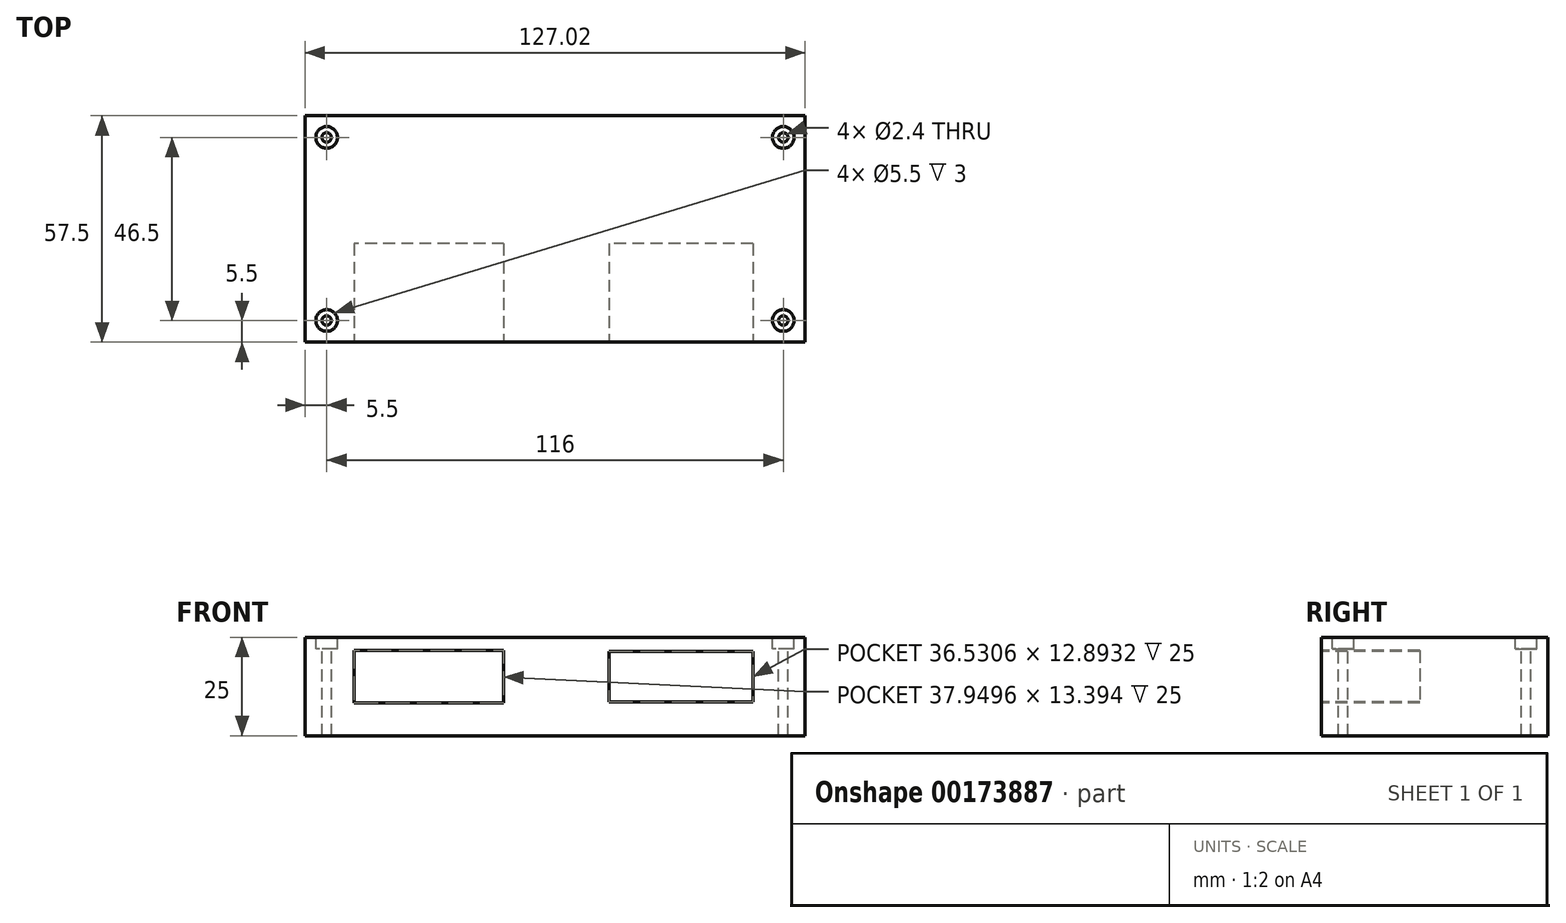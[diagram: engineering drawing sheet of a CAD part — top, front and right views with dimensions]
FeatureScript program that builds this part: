
annotation { "Feature Type Name" : "Feature", "Feature Type Description" : "" }
export const myFeature = defineFeature(function(context is Context, id is Id, definition is map)
    precondition{}
    {
        {
            var Q0;
            Q0=qCreatedBy(makeId("Top.planeOp"),FACE);
            var sketch = newSketch(context, id + "F0", { "sketchPlane" : qUnion([Q0])});
            skLineSegment(sketch, "E0.bottom", {"start": v(0, 0) * mm, "end": v(127.02, 0) * mm});
            skLineSegment(sketch, "E0.top", {"start": v(0, 57.5) * mm, "end": v(127.02, 57.5) * mm});
            skLineSegment(sketch, "E0.left", {"start": v(0, 0) * mm, "end": v(0, 57.5) * mm});
            skLineSegment(sketch, "E0.right", {"start": v(127.02, 0) * mm, "end": v(127.02, 57.5) * mm});
            skSolve(sketch);
        }
        {
            var Q0;
            Q0=makeQuery(id+"F0.imprint","IMPRINT",FACE,{"disambiguationData":[TD([[makeQuery(id+"F0.imprint","IMPRINT",EDGE,{"derivedFrom":sQuery(id+"F0.wireOp",EDGE,"E0.bottom")}),1.0]])]});
            extrude(context, id + "F1", {"entities" : qUnion([Q0]), "depth" : 25 * mm});
        }
        {
            var Q0;
            Q0=makeQuery(id+"F1.opExtrude","SWEPT_FACE",FACE,{"disambiguationData":[OSD([sQuery(id+"F0.wireOp",EDGE,"E0.bottom")])]});
            var sketch = newSketch(context, id + "F2", { "sketchPlane" : qUnion([Q0])});
            skLineSegment(sketch, "E1.bottom", {"start": v(50.47, 21.7) * mm, "end": v(12.53, 21.7) * mm});
            skLineSegment(sketch, "E1.top", {"start": v(50.47, 8.3) * mm, "end": v(12.53, 8.3) * mm});
            skLineSegment(sketch, "E1.left", {"start": v(50.47, 21.7) * mm, "end": v(50.47, 8.3) * mm});
            skLineSegment(sketch, "E1.right", {"start": v(12.53, 21.7) * mm, "end": v(12.53, 8.3) * mm});
            skPoint(sketch, "E1.middle", {"position": v(31.5, 15) * mm});
            skLineSegment(sketch, "E2.bottom", {"start": v(113.77, 21.45) * mm, "end": v(77.23, 21.45) * mm});
            skLineSegment(sketch, "E2.top", {"start": v(113.77, 8.55) * mm, "end": v(77.23, 8.55) * mm});
            skLineSegment(sketch, "E2.left", {"start": v(113.77, 21.45) * mm, "end": v(113.77, 8.55) * mm});
            skLineSegment(sketch, "E2.right", {"start": v(77.23, 21.45) * mm, "end": v(77.23, 8.55) * mm});
            skPoint(sketch, "E2.middle", {"position": v(95.5, 15) * mm});
            skSolve(sketch);
        }
        {
            var Q0;
            Q0 = qSketchRegion(id + "F2", true);
            extrude(context, id + "F3", {"entities" : qUnion([Q0]), "operationType" : NewBodyOperationType.REMOVE, "oppositeDirection" : true, "depth" : 25 * mm});
        }
        {
            var Q0;
            Q0=makeQuery(id+"F1.opExtrude","CAP_FACE",FACE,{"disambiguationData":[OSD([sQuery(id+"F0.wireOp",EDGE,"E0.bottom"),sQuery(id+"F0.wireOp",EDGE,"E0.top"),sQuery(id+"F0.wireOp",EDGE,"E0.left"),sQuery(id+"F0.wireOp",EDGE,"E0.right")])],"isStart":false});
            var sketch = newSketch(context, id + "F4", { "sketchPlane" : qUnion([Q0])});
            skLineSegment(sketch, "E3.bottom", {"start": v(0, 0) * mm, "end": v(8.5, 0) * mm});
            skLineSegment(sketch, "E3.top", {"start": v(0, 8.5) * mm, "end": v(8.5, 8.5) * mm});
            skLineSegment(sketch, "E3.left", {"start": v(0, 0) * mm, "end": v(0, 8.5) * mm});
            skLineSegment(sketch, "E3.right", {"start": v(8.5, 0) * mm, "end": v(8.5, 8.5) * mm});
            skLineSegment(sketch, "E4.0.1.0", {"start": v(0, 57.5) * mm, "end": v(8.5, 57.5) * mm});
            skLineSegment(sketch, "E4.0.1.1", {"start": v(0, 49) * mm, "end": v(0, 57.5) * mm});
            skLineSegment(sketch, "E4.0.1.2", {"start": v(8.5, 49) * mm, "end": v(8.5, 57.5) * mm});
            skLineSegment(sketch, "E4.0.1.3", {"start": v(0, 49) * mm, "end": v(8.5, 49) * mm});
            skLineSegment(sketch, "E4.1.0.0", {"start": v(118.5, 8.5) * mm, "end": v(127, 8.5) * mm});
            skLineSegment(sketch, "E4.1.0.1", {"start": v(118.5, 0) * mm, "end": v(118.5, 8.5) * mm});
            skLineSegment(sketch, "E4.1.0.2", {"start": v(127, 0) * mm, "end": v(127, 8.5) * mm});
            skLineSegment(sketch, "E4.1.0.3", {"start": v(118.5, 0) * mm, "end": v(127, 0) * mm});
            skLineSegment(sketch, "E4.1.1.0", {"start": v(118.5, 57.5) * mm, "end": v(127, 57.5) * mm});
            skLineSegment(sketch, "E4.1.1.1", {"start": v(118.5, 49) * mm, "end": v(118.5, 57.5) * mm});
            skLineSegment(sketch, "E4.1.1.2", {"start": v(127, 49) * mm, "end": v(127, 57.5) * mm});
            skLineSegment(sketch, "E4.1.1.3", {"start": v(118.5, 49) * mm, "end": v(127, 49) * mm});
            skLineSegment(sketch, "E4.direction1", {"start": v(0, 8.5) * mm, "end": v(118.5, 8.5) * mm, "construction": true});
            skLineSegment(sketch, "E4.direction2", {"start": v(0, 8.5) * mm, "end": v(0, 57.5) * mm, "construction": true});
            skSolve(sketch);
        }
        {
            var Q0;
            Q0 = qSketchRegion(id + "F4", true);
            extrude(context, id + "F5", {"entities" : qUnion([Q0]), "operationType" : NewBodyOperationType.ADD, "oppositeDirection" : true, "depth" : 25 * mm});
        }
        {
            var Q0;
            Q0=makeQuery(id+"F1.opExtrude","CAP_FACE",FACE,{"disambiguationData":[OSD([sQuery(id+"F0.wireOp",EDGE,"E0.bottom"),sQuery(id+"F0.wireOp",EDGE,"E0.top"),sQuery(id+"F0.wireOp",EDGE,"E0.left"),sQuery(id+"F0.wireOp",EDGE,"E0.right")])],"isStart":false});
            var sketch = newSketch(context, id + "F6", { "sketchPlane" : qUnion([Q0])});
            skPoint(sketch, "E5", {"position": v(5.5, 5.5) * mm});
            skPoint(sketch, "E6.0.1.0", {"position": v(5.5, 52) * mm});
            skPoint(sketch, "E6.1.0.0", {"position": v(121.5, 5.5) * mm});
            skPoint(sketch, "E6.1.1.0", {"position": v(121.5, 52) * mm});
            skLineSegment(sketch, "E6.direction1", {"start": v(5.5, 5.5) * mm, "end": v(121.5, 5.5) * mm, "construction": true});
            skLineSegment(sketch, "E6.direction2", {"start": v(5.5, 5.5) * mm, "end": v(5.5, 52) * mm, "construction": true});
            skSolve(sketch);
        }
        {
            var Q0;
            Q0=sQuery(id+"F6.wireOp",VERTEX,"E6.0.1.0");
            var Q1;
            Q1=sQuery(id+"F6.wireOp",VERTEX,"E6.1.1.0");
            var Q2;
            Q2=sQuery(id+"F6.wireOp",VERTEX,"E5");
            var Q3;
            Q3=sQuery(id+"F6.wireOp",VERTEX,"E6.1.0.0");
            var Q4;
            Q4=makeQuery(id+"F1.opExtrude","SWEPT_BODY",BODY,{"disambiguationData":[OSD([sQuery(id+"F0.wireOp",EDGE,"E0.bottom"),sQuery(id+"F0.wireOp",EDGE,"E0.top"),sQuery(id+"F0.wireOp",EDGE,"E0.left"),sQuery(id+"F0.wireOp",EDGE,"E0.right")])]});
            hole(context, id + "F7", {"style" : HoleStyle.C_BORE, "endStyle" : HoleEndStyle.THROUGH, "holeDiameter" : 2.4 * mm, "cBoreDiameter" : 5.5 * mm, "cBoreDepth" : 3 * mm, "locations" : qUnion([Q0, Q1, Q2, Q3]), "scope" : qUnion([Q4]), "isTappedThrough" : true});
        }
    });
